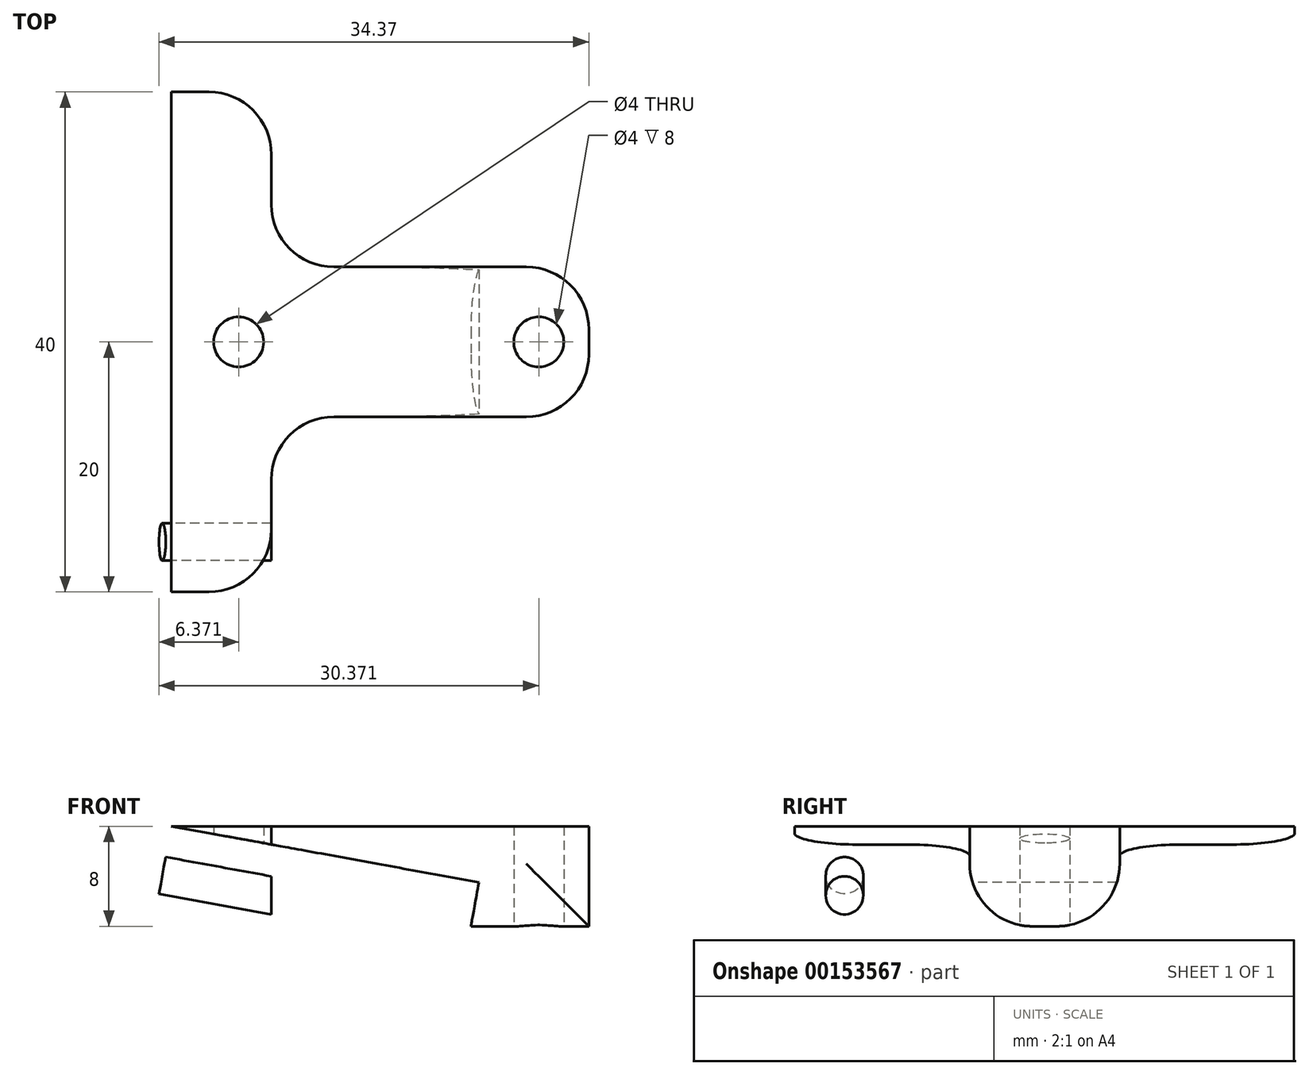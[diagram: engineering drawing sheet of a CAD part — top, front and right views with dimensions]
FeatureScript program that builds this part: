
annotation { "Feature Type Name" : "Feature", "Feature Type Description" : "" }
export const myFeature = defineFeature(function(context is Context, id is Id, definition is map)
    precondition{}
    {
        {
            var Q0;
            Q0=qCreatedBy(makeId("Top.planeOp"),FACE);
            var sketch = newSketch(context, id + "F0", { "sketchPlane" : qUnion([Q0])});
            skCircle(sketch, "E0", {"center": v(-12.47, 0) * mm, "radius": 2 * mm});
            skCircle(sketch, "E1", {"center": v(11.53, 0) * mm, "radius": 2 * mm});
            skLineSegment(sketch, "E2.bottom", {"start": v(-17.85, 20) * mm, "end": v(-9.85, 20) * mm});
            skLineSegment(sketch, "E2.top", {"start": v(-17.85, -20) * mm, "end": v(-9.85, -20) * mm});
            skLineSegment(sketch, "E2.left", {"start": v(-9.85, 20) * mm, "end": v(-9.85, -20) * mm});
            skLineSegment(sketch, "E2.right", {"start": v(-17.85, 20) * mm, "end": v(-17.85, -20) * mm});
            skLineSegment(sketch, "E3.bottom", {"start": v(15.53, 6) * mm, "end": v(-17.85, 6) * mm});
            skLineSegment(sketch, "E3.top", {"start": v(15.53, -6) * mm, "end": v(-17.85, -6) * mm});
            skLineSegment(sketch, "E3.left", {"start": v(15.53, 6) * mm, "end": v(15.53, -6) * mm});
            skLineSegment(sketch, "E3.right", {"start": v(-17.85, 6) * mm, "end": v(-17.85, -6) * mm});
            skPoint(sketch, "E4", {"position": v(-17.85, 0) * mm});
            skSolve(sketch);
        }
        {
            var Q0;
            {var subQ0=sQuery(id+"F0.wireOp",EDGE,"E2.bottom");Q0=makeQuery(id+"F0.imprint","IMPRINT",FACE,{"disambiguationData":[TD([[makeQuery(id+"F0.imprint","IMPRINT",EDGE,{"derivedFrom":subQ0}),-1.0]])]});}
            var Q1;
            Q1=makeQuery(id+"F0.imprint","IMPRINT",FACE,{"disambiguationData":[TD([[makeQuery(id+"F0.imprint","IMPRINT",EDGE,{"derivedFrom":sQuery(id+"F0.wireOp",EDGE,"E0")}),-1.0]])]});
            var Q2;
            {var subQ0=sQuery(id+"F0.wireOp",EDGE,"E2.top");Q2=makeQuery(id+"F0.imprint","IMPRINT",FACE,{"disambiguationData":[TD([[makeQuery(id+"F0.imprint","IMPRINT",EDGE,{"derivedFrom":subQ0}),1.0]])]});}
            var Q3;
            Q3=makeQuery(id+"F0.imprint","IMPRINT",FACE,{"disambiguationData":[TD([[makeQuery(id+"F0.imprint","IMPRINT",EDGE,{"derivedFrom":sQuery(id+"F0.wireOp",EDGE,"E1")}),-1.0]])]});
            extrude(context, id + "F1", {"entities" : qUnion([Q0, Q1, Q2, Q3]), "depth" : 8 * mm});
        }
        {
            var Q0;
            Q0=makeQuery(id+"F1.opExtrude","SWEPT_FACE",FACE,{"disambiguationData":[OSD([sQuery(id+"F0.wireOp",EDGE,"E2.top")])]});
            var sketch = newSketch(context, id + "F2", { "sketchPlane" : qUnion([Q0])});
            skLineSegment(sketch, "E5", {"start": v(-17.85, 8) * mm, "end": v(-25.03, -31.35) * mm});
            skLineSegment(sketch, "E6", {"start": v(-25.03, -31.35) * mm, "end": v(-35.85, -29.38) * mm});
            skLineSegment(sketch, "E7", {"start": v(-35.85, -29.38) * mm, "end": v(-28.67, 9.97) * mm});
            skLineSegment(sketch, "E8", {"start": v(-28.67, 9.97) * mm, "end": v(-17.85, 8) * mm});
            skLineSegment(sketch, "E9", {"start": v(-17.85, 0) * mm, "end": v(-19.31, 0) * mm});
            skSolve(sketch);
        }
        {
            var Q0;
            {var subQ3=sQuery(id+"F2.wireOp",EDGE,"E9");Q0=makeQuery(id+"F2.imprint","IMPRINT",FACE,{"disambiguationData":[TD([[makeQuery(id+"F2.imprint","IMPRINT",EDGE,{"derivedFrom":subQ3}),-1.0]])]});}
            extrude(context, id + "F3", {"entities" : qUnion([Q0]), "operationType" : NewBodyOperationType.ADD, "oppositeDirection" : true, "depth" : 40 * mm});
        }
        {
            var Q0;
            Q0=makeQuery(id+"F3.opExtrude","SWEPT_FACE",FACE,{"disambiguationData":[OSD([sQuery(id+"F2.wireOp",EDGE,"E5")])]});
            var sketch = newSketch(context, id + "F4", { "sketchPlane" : qUnion([Q0])});
            skLineSegment(sketch, "E10", {"start": v(-20, 4.67) * mm, "end": v(-20, -3.47) * mm});
            skCircle(sketch, "E11", {"center": v(-16, 0.67) * mm, "radius": 1.5 * mm});
            skCircle(sketch, "E12.MirrorC", {"center": v(16, 0.67) * mm, "radius": 1.5 * mm});
            skSolve(sketch);
        }
        {
            var Q0;
            Q0=makeQuery(id+"F4.imprint","IMPRINT",FACE,{"disambiguationData":[TD([[makeQuery(id+"F4.imprint","IMPRINT",EDGE,{"derivedFrom":sQuery(id+"F4.wireOp",EDGE,"E12.MirrorC")}),-1.0]])]});
            var Q1;
            Q1=makeQuery(id+"F4.imprint","IMPRINT",FACE,{"disambiguationData":[TD([[makeQuery(id+"F4.imprint","IMPRINT",EDGE,{"derivedFrom":sQuery(id+"F4.wireOp",EDGE,"E11")}),1.0]])]});
            extrude(context, id + "F5", {"entities" : qUnion([Q0, Q1]), "operationType" : NewBodyOperationType.REMOVE, "oppositeDirection" : true, "depth" : 25 * mm});
        }
        {
            var Q0;
            Q0=makeQuery(id+"F1.opExtrude","CAP_FACE",FACE,{"disambiguationData":[OSD([sQuery(id+"F0.wireOp",EDGE,"E0"),sQuery(id+"F0.wireOp",EDGE,"E1"),sQuery(id+"F0.wireOp",EDGE,"E2.bottom"),sQuery(id+"F0.wireOp",EDGE,"E2.top"),sQuery(id+"F0.wireOp",EDGE,"E2.left"),sQuery(id+"F0.wireOp",EDGE,"E2.right"),sQuery(id+"F0.wireOp",EDGE,"E3.bottom"),sQuery(id+"F0.wireOp",EDGE,"E3.top"),sQuery(id+"F0.wireOp",EDGE,"E3.left"),sQuery(id+"F0.wireOp",EDGE,"E3.right")])],"isStart":false});
            var sketch = newSketch(context, id + "F6", { "sketchPlane" : qUnion([Q0])});
            skLineSegment(sketch, "E13.bottom", {"start": v(15.53, -6) * mm, "end": v(-38, -6) * mm});
            skLineSegment(sketch, "E13.top", {"start": v(15.53, 6) * mm, "end": v(-38, 6) * mm});
            skLineSegment(sketch, "E13.left", {"start": v(15.53, -6) * mm, "end": v(15.53, 6) * mm});
            skLineSegment(sketch, "E13.right", {"start": v(-38, -6) * mm, "end": v(-38, 6) * mm});
            skSolve(sketch);
        }
        {
            var Q0;
            Q0=makeQuery(id+"F6.imprint","IMPRINT",FACE,{"disambiguationData":[TD([[makeQuery(id+"F6.imprint","IMPRINT",EDGE,{"derivedFrom":makeQuery(id+"F1.opExtrude","CAP_EDGE",EDGE,{"disambiguationData":[OSD([sQuery(id+"F0.wireOp",EDGE,"E0")])],"isStart":false})}),1.0]])]});
            var Q1;
            Q1=makeQuery(id+"F6.imprint","IMPRINT",FACE,{"disambiguationData":[TD([[makeQuery(id+"F6.imprint","IMPRINT",EDGE,{"derivedFrom":makeQuery(id+"F1.opExtrude","CAP_EDGE",EDGE,{"disambiguationData":[OSD([sQuery(id+"F0.wireOp",EDGE,"E1")])],"isStart":false})}),1.0]])]});
            extrude(context, id + "F7", {"entities" : qUnion([Q0, Q1]), "operationType" : NewBodyOperationType.REMOVE, "oppositeDirection" : true, "depth" : 4 * mm});
        }
        {
            var Q0;
            Q0=makeQuery(id+"F1.opExtrude","SWEPT_EDGE",EDGE,{"disambiguationData":[OSD([sQuery(id+"F0.wireOp",EDGE,"E3.bottom"),sQuery(id+"F0.wireOp",EDGE,"E3.left")])]});
            var Q1;
            Q1=makeQuery(id+"F1.opExtrude","SWEPT_EDGE",EDGE,{"disambiguationData":[OSD([sQuery(id+"F0.wireOp",EDGE,"E3.top"),sQuery(id+"F0.wireOp",EDGE,"E3.left")])]});
            var Q2;
            Q2=makeQuery(id+"F1.opExtrude","SWEPT_EDGE",EDGE,{"disambiguationData":[OSD([sQuery(id+"F0.wireOp",EDGE,"E2.left"),sQuery(id+"F0.wireOp",EDGE,"E3.top")])]});
            var Q3;
            Q3=makeQuery(id+"F1.opExtrude","SWEPT_EDGE",EDGE,{"disambiguationData":[OSD([sQuery(id+"F0.wireOp",EDGE,"E2.top"),sQuery(id+"F0.wireOp",EDGE,"E2.left")])]});
            var Q4;
            Q4=makeQuery(id+"F1.opExtrude","SWEPT_EDGE",EDGE,{"disambiguationData":[OSD([sQuery(id+"F0.wireOp",EDGE,"E2.left"),sQuery(id+"F0.wireOp",EDGE,"E3.bottom")])]});
            var Q5;
            Q5=makeQuery(id+"F1.opExtrude","SWEPT_EDGE",EDGE,{"disambiguationData":[OSD([sQuery(id+"F0.wireOp",EDGE,"E2.bottom"),sQuery(id+"F0.wireOp",EDGE,"E2.left")])]});
            var Q6;
            Q6=makeQuery(id+"F1.opExtrude","CAP_EDGE",EDGE,{"disambiguationData":[OSD([sQuery(id+"F0.wireOp",EDGE,"E3.bottom")])],"isStart":true});
            var Q7;
            Q7=makeQuery(id+"F1.opExtrude","CAP_EDGE",EDGE,{"disambiguationData":[OSD([sQuery(id+"F0.wireOp",EDGE,"E3.top")])],"isStart":true});
            fillet(context, id + "F8", {"entities" : qUnion([Q0, Q1, Q2, Q3, Q4, Q5, Q6, Q7]), "radius" : 5 * mm, "tangentPropagation" : true, "allowEdgeOverflow" : false});
        }
    });
